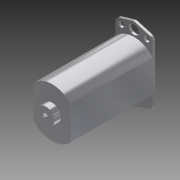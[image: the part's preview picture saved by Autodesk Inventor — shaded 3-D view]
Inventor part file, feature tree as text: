
AUTODESK INVENTOR PART (.ipt)
format: ipt  version: 2016 SP1 (Build 200210100, 210)  size: 119,296 bytes
history: native  units: in
note: dims shown in document units (in); Inventor stores cm internally (conversion verified against a paired STEP export)
features: other x2, imported_body x2, fillet x1
ambient origin geometry x8: Origin, YZ Plane, XZ Plane, XY Plane, X Axis, Y Axis, Z Axis, Center Point
bodies: Body1 (feature_tree), Body2 (feature_tree)
feature tree (5):
  fillet  "Fillet1"  [1 undecoded]
  other  "AM-2235 motor.ipt1"
  other  "Boss-Extrude4"
  imported_body  "Base1"
  imported_body  "Base2"
note: 1 required parameter value undecoded (feature->parameter linkage not recoverable at this tier; creation-order binding heuristic only, values carry confidence <= 0.55)
